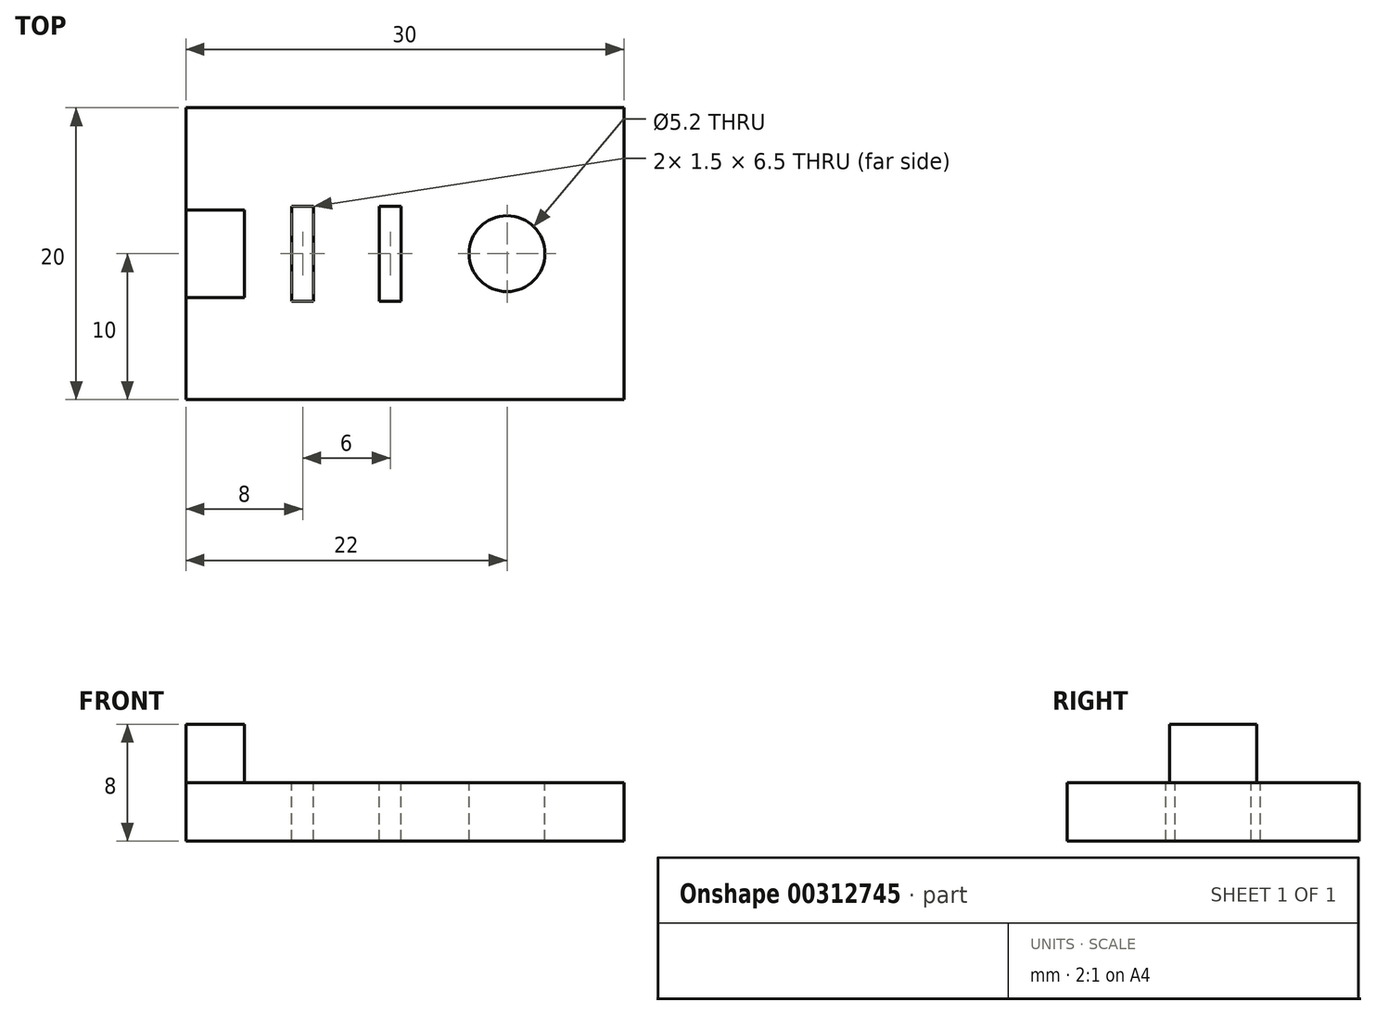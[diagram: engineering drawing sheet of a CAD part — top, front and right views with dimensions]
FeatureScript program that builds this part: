
annotation { "Feature Type Name" : "Feature", "Feature Type Description" : "" }
export const myFeature = defineFeature(function(context is Context, id is Id, definition is map)
    precondition{}
    {
        {
            var Q0;
            Q0=qCreatedBy(makeId("Top.planeOp"),FACE);
            var sketch = newSketch(context, id + "F0", { "sketchPlane" : qUnion([Q0])});
            skLineSegment(sketch, "E0.bottom", {"start": v(-15, 10) * mm, "end": v(15, 10) * mm});
            skLineSegment(sketch, "E0.top", {"start": v(-15, -10) * mm, "end": v(15, -10) * mm});
            skLineSegment(sketch, "E0.left", {"start": v(-15, 10) * mm, "end": v(-15, -10) * mm});
            skLineSegment(sketch, "E0.right", {"start": v(15, 10) * mm, "end": v(15, -10) * mm});
            skPoint(sketch, "E0.middle", {"position": v(0, 0) * mm});
            skSolve(sketch);
        }
        {
            var Q0;
            Q0 = qSketchRegion(id + "F0", true);
            extrude(context, id + "F1", {"entities" : qUnion([Q0]), "depth" : 4 * mm});
        }
        {
            var Q0;
            Q0=makeQuery(id+"F1.opExtrude","CAP_FACE",FACE,{"disambiguationData":[OSD([sQuery(id+"F0.wireOp",EDGE,"E0.bottom"),sQuery(id+"F0.wireOp",EDGE,"E0.top"),sQuery(id+"F0.wireOp",EDGE,"E0.left"),sQuery(id+"F0.wireOp",EDGE,"E0.right")])],"isStart":false});
            var sketch = newSketch(context, id + "F2", { "sketchPlane" : qUnion([Q0])});
            skCircle(sketch, "E1", {"center": v(7, 0) * mm, "radius": 2.6 * mm});
            skLineSegment(sketch, "E2.bottom", {"start": v(-1.75, 3.25) * mm, "end": v(-0.25, 3.25) * mm});
            skLineSegment(sketch, "E2.top", {"start": v(-1.75, -3.25) * mm, "end": v(-0.25, -3.25) * mm});
            skLineSegment(sketch, "E2.left", {"start": v(-1.75, 3.25) * mm, "end": v(-1.75, -3.25) * mm});
            skLineSegment(sketch, "E2.right", {"start": v(-0.25, 3.25) * mm, "end": v(-0.25, -3.25) * mm});
            skPoint(sketch, "E2.middle", {"position": v(-1, 0) * mm});
            skLineSegment(sketch, "E3.bottom", {"start": v(-6.25, 3.25) * mm, "end": v(-7.75, 3.25) * mm});
            skLineSegment(sketch, "E3.top", {"start": v(-6.25, -3.25) * mm, "end": v(-7.75, -3.25) * mm});
            skLineSegment(sketch, "E3.left", {"start": v(-6.25, 3.25) * mm, "end": v(-6.25, -3.25) * mm});
            skLineSegment(sketch, "E3.right", {"start": v(-7.75, 3.25) * mm, "end": v(-7.75, -3.25) * mm});
            skPoint(sketch, "E3.middle", {"position": v(-7, 0) * mm});
            skPoint(sketch, "E3.middle.positionSnap0", {"position": v(-1.75, 0) * mm});
            skPoint(sketch, "E3.centerSnap0", {"position": v(-1.75, 0) * mm});
            skSolve(sketch);
        }
        {
            var Q0;
            Q0 = qSketchRegion(id + "F2", true);
            extrude(context, id + "F3", {"entities" : qUnion([Q0]), "operationType" : NewBodyOperationType.REMOVE, "endBound" : BoundingType.THROUGH_ALL, "oppositeDirection" : true, "depth" : 25 * mm});
        }
        {
            var Q0;
            Q0=makeQuery(id+"F1.opExtrude","CAP_FACE",FACE,{"disambiguationData":[OSD([sQuery(id+"F0.wireOp",EDGE,"E0.bottom"),sQuery(id+"F0.wireOp",EDGE,"E0.top"),sQuery(id+"F0.wireOp",EDGE,"E0.left"),sQuery(id+"F0.wireOp",EDGE,"E0.right")])],"isStart":false});
            var sketch = newSketch(context, id + "F4", { "sketchPlane" : qUnion([Q0])});
            skLineSegment(sketch, "E4.bottom", {"start": v(-15, 3) * mm, "end": v(-11, 3) * mm});
            skLineSegment(sketch, "E4.top", {"start": v(-15, -3) * mm, "end": v(-11, -3) * mm});
            skLineSegment(sketch, "E4.left", {"start": v(-15, 3) * mm, "end": v(-15, -3) * mm});
            skLineSegment(sketch, "E4.right", {"start": v(-11, 3) * mm, "end": v(-11, -3) * mm});
            skPoint(sketch, "E5", {"position": v(-15, 0) * mm});
            skSolve(sketch);
        }
        {
            var Q0;
            Q0 = qSketchRegion(id + "F4", true);
            extrude(context, id + "F5", {"entities" : qUnion([Q0]), "operationType" : NewBodyOperationType.ADD, "depth" : 4 * mm});
        }
    });
